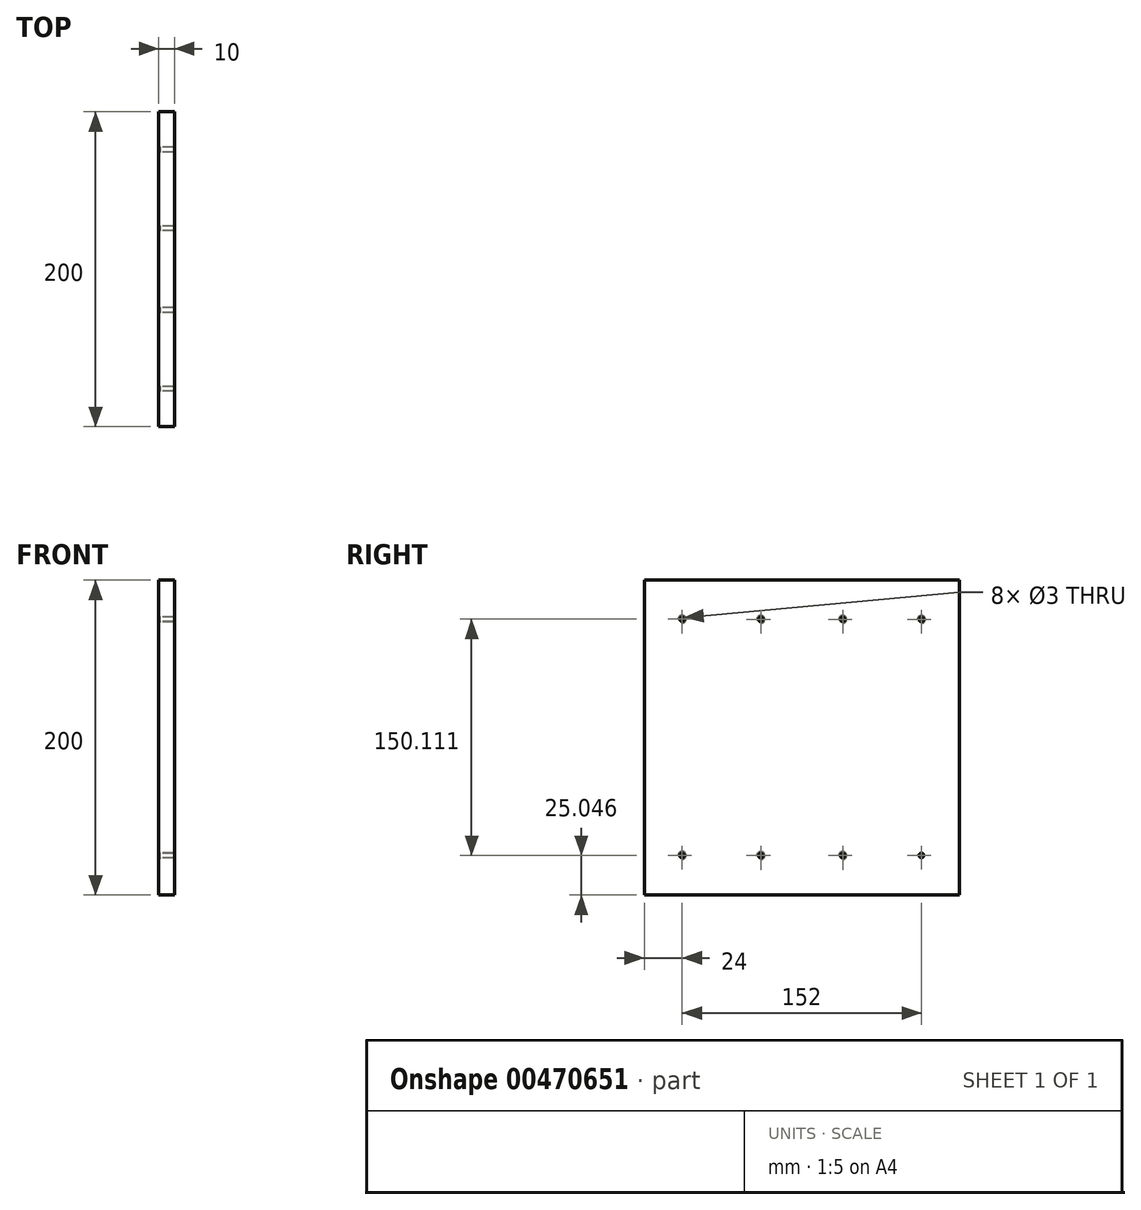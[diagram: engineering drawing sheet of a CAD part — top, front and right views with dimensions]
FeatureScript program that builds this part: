
annotation { "Feature Type Name" : "Feature", "Feature Type Description" : "" }
export const myFeature = defineFeature(function(context is Context, id is Id, definition is map)
    precondition{}
    {
        {
            var Q0;
            Q0=qCreatedBy(makeId("Right.planeOp"),FACE);
            var sketch = newSketch(context, id + "F0", { "sketchPlane" : qUnion([Q0])});
            skLineSegment(sketch, "E0.bottom", {"start": v(100, 100) * mm, "end": v(-100, 100) * mm});
            skLineSegment(sketch, "E0.top", {"start": v(100, -100) * mm, "end": v(-100, -100) * mm});
            skLineSegment(sketch, "E0.left", {"start": v(100, 100) * mm, "end": v(100, -100) * mm});
            skLineSegment(sketch, "E0.right", {"start": v(-100, 100) * mm, "end": v(-100, -100) * mm});
            skPoint(sketch, "E0.middle", {"position": v(0, 0) * mm});
            skCircle(sketch, "E1", {"center": v(-76, 75.16) * mm, "radius": 1.5 * mm});
            skCircle(sketch, "E2", {"center": v(-76, -74.84) * mm, "radius": 1.5 * mm});
            skCircle(sketch, "E3", {"center": v(-26, 75.05) * mm, "radius": 1.5 * mm});
            skCircle(sketch, "E4", {"center": v(-26, -74.95) * mm, "radius": 1.5 * mm});
            skCircle(sketch, "E5", {"center": v(76, 75.06) * mm, "radius": 1.5 * mm});
            skCircle(sketch, "E6", {"center": v(26, 75.06) * mm, "radius": 1.5 * mm});
            skCircle(sketch, "E7", {"center": v(76, -74.84) * mm, "radius": 1.5 * mm});
            skCircle(sketch, "E8", {"center": v(26, -74.94) * mm, "radius": 1.5 * mm});
            skSolve(sketch);
        }
        {
            var Q0;
            Q0=makeQuery(id+"F0.imprint","IMPRINT",FACE,{"disambiguationData":[TD([[makeQuery(id+"F0.imprint","IMPRINT",EDGE,{"derivedFrom":sQuery(id+"F0.wireOp",EDGE,"E0.bottom")}),1.0]])]});
            extrude(context, id + "F1", {"entities" : qUnion([Q0]), "depth" : 10 * mm});
        }
        {
            var Q0;
            Q0=makeQuery(id+"F1.opExtrude","CAP_EDGE",EDGE,{"disambiguationData":[OSD([sQuery(id+"F0.wireOp",EDGE,"E2")])],"isStart":true});
            var Q1;
            Q1=makeQuery(id+"F1.opExtrude","CAP_EDGE",EDGE,{"disambiguationData":[OSD([sQuery(id+"F0.wireOp",EDGE,"E4")])],"isStart":true});
            var Q2;
            Q2=makeQuery(id+"F1.opExtrude","CAP_EDGE",EDGE,{"disambiguationData":[OSD([sQuery(id+"F0.wireOp",EDGE,"E3")])],"isStart":true});
            var Q3;
            Q3=makeQuery(id+"F1.opExtrude","CAP_EDGE",EDGE,{"disambiguationData":[OSD([sQuery(id+"F0.wireOp",EDGE,"E1")])],"isStart":true});
            chamfer(context, id + "F2", {"entities" : qUnion([Q0, Q1, Q2, Q3]), "width" : 1 * mm, "tangentPropagation" : true});
        }
        {
            var Q0;
            Q0=makeQuery(id+"F1.opExtrude","CAP_EDGE",EDGE,{"disambiguationData":[OSD([sQuery(id+"F0.wireOp",EDGE,"E8")])],"isStart":true});
            var Q1;
            Q1=makeQuery(id+"F1.opExtrude","CAP_EDGE",EDGE,{"disambiguationData":[OSD([sQuery(id+"F0.wireOp",EDGE,"E6")])],"isStart":true});
            var Q2;
            Q2=makeQuery(id+"F1.opExtrude","CAP_EDGE",EDGE,{"disambiguationData":[OSD([sQuery(id+"F0.wireOp",EDGE,"E5")])],"isStart":true});
            chamfer(context, id + "F3", {"entities" : qUnion([Q0, Q1, Q2]), "width" : 1 * mm, "tangentPropagation" : true});
        }
    });
